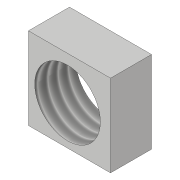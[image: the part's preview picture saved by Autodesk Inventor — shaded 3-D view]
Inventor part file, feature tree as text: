
AUTODESK INVENTOR PART (.ipt)
format: ipt  version: 2019 (Build 230136000, 136)  size: 90,624 bytes
history: native  units: in
note: dims shown in document units (in); Inventor stores cm internally (conversion verified against a paired STEP export)
features: extrude x2, sketch x2, thread x1
ambient origin geometry x8: Origin, YZ Plane, XZ Plane, XY Plane, X Axis, Y Axis, Z Axis, Center Point
bodies: Solid1 (feature_tree)
feature tree (5):
  extrude  "Extrusion1"  Depth=0.3937in
  extrude  "Extrusion2"  Depth=0.3937in
  thread  "Thread1"  [1 undecoded]
  sketch  "Sketch1"  dims[d0=0.3937in d1=0.3937in]
  sketch  "Sketch2"  dims[d2=0.1969in d3=0.0in d4=0.315in d5=0.1969in d6=0.0in d7=0.3937in d8=0.0in]
note: 1 required parameter value undecoded (feature->parameter linkage not recoverable at this tier; creation-order binding heuristic only, values carry confidence <= 0.55)
